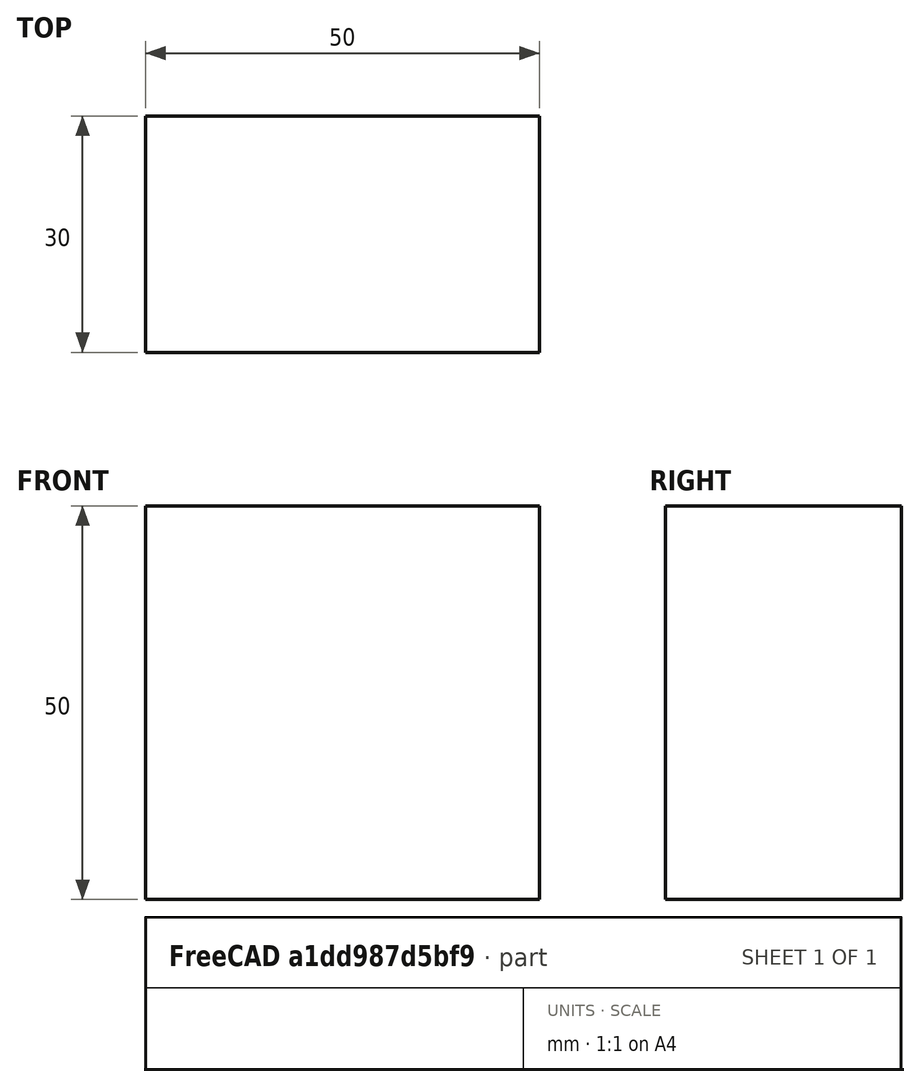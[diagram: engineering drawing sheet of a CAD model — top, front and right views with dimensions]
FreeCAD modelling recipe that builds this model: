
FCSTD DOCUMENT  (FreeCAD 0.15R4671 (Git))
Label: Flat Bar 50x30 EN10058 S235JR
License: All rights reserved
LicenseURL: http://en.wikipedia.org/wiki/All_rights_reserved
objects: Sketcher::SketchObject×1, Part::Extrusion×1
note: 2 computed .brp shape members not serialized (recipe doc carries the construction recipe); baked Part::Feature solids carry a one-line shape summary decoded from their .brp

FEATURE [Sketcher::SketchObject] Sketch
  sketch-geometry (4):
    g0: LineSegment StartX=-25 StartY=-15 StartZ=0 EndX=25 EndY=-15 EndZ=0
    g1: LineSegment StartX=25 StartY=-15 StartZ=0 EndX=25 EndY=15 EndZ=0
    g2: LineSegment StartX=25 StartY=15 StartZ=0 EndX=-25 EndY=15 EndZ=0
    g3: LineSegment StartX=-25 StartY=15 StartZ=0 EndX=-25 EndY=-15 EndZ=0
  constraints (12):
    c: Coincident(g0,g1)
    c: Coincident(g1,g2)
    c: Coincident(g2,g3)
    c: Coincident(g3,g0)
    c: Horizontal(g0)
    c: Horizontal(g2)
    c: Vertical(g1)
    c: Vertical(g3)
    c: Symmetric(g1,g2,g-2)
    c: Symmetric(g0,g1,g-1)
    c: DistanceY(g1) = 30
    c: DistanceX(g0) = 50
FEATURE [Part::Extrusion] Extrude  label="Flat Bar 50x30 EN10058 S235JR"
  Base = -> Sketch
  Dir = (0,0,50)
  Solid = true
